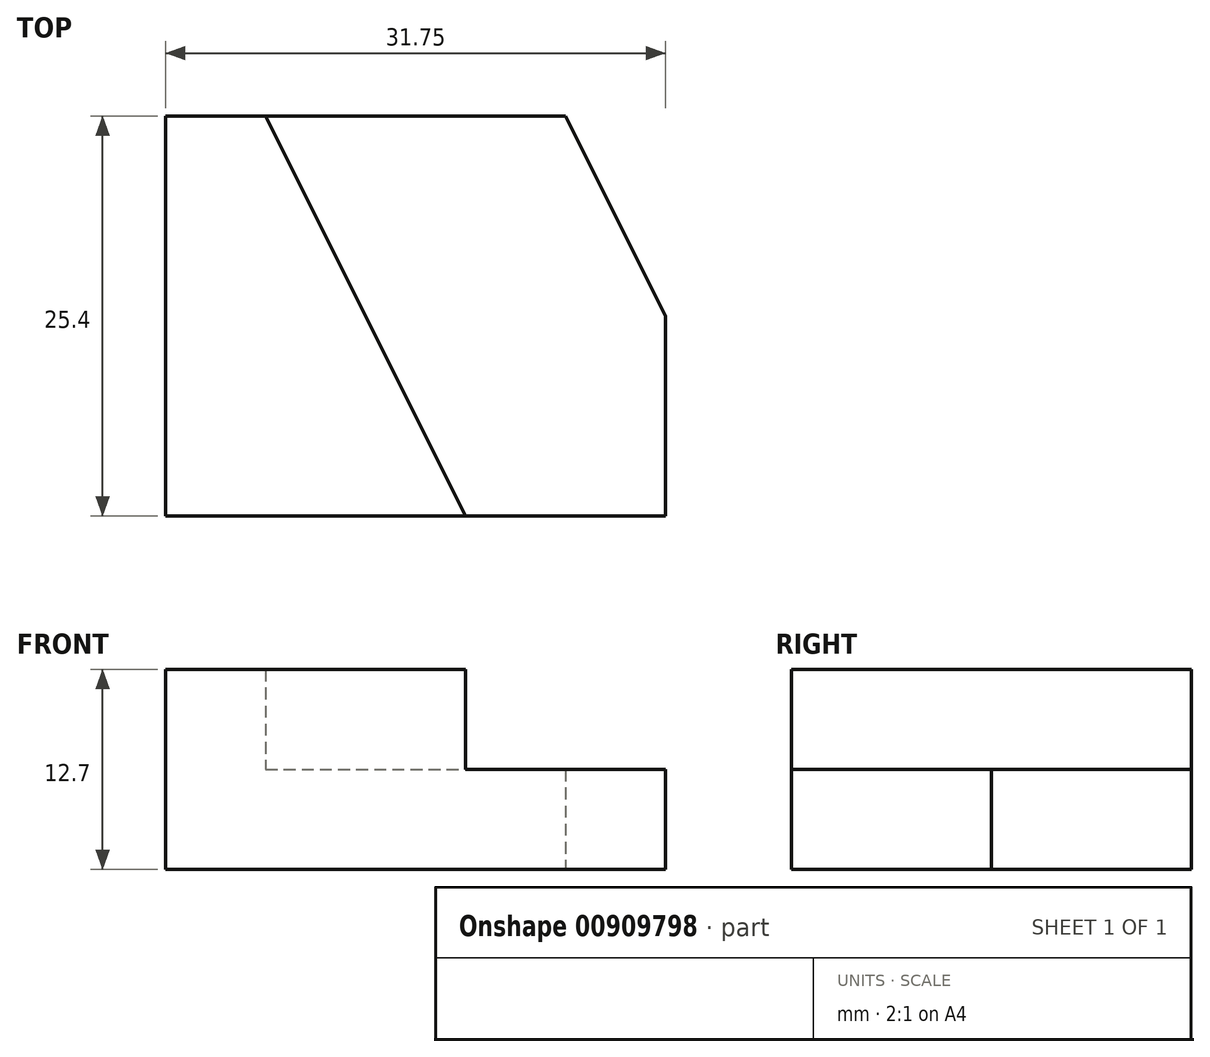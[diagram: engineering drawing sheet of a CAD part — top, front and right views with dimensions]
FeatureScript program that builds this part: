
annotation { "Feature Type Name" : "Feature", "Feature Type Description" : "" }
export const myFeature = defineFeature(function(context is Context, id is Id, definition is map)
    precondition{}
    {
        {
            var Q0;
            Q0=qCreatedBy(makeId("Top.planeOp"),FACE);
            var sketch = newSketch(context, id + "F0", { "sketchPlane" : qUnion([Q0])});
            skLineSegment(sketch, "E0", {"start": v(-58.15, 50.5) * mm, "end": v(-32.75, 50.5) * mm});
            skLineSegment(sketch, "E1", {"start": v(-58.15, 50.5) * mm, "end": v(-58.15, 25.1) * mm});
            skLineSegment(sketch, "E2", {"start": v(-58.15, 25.1) * mm, "end": v(-26.4, 25.1) * mm});
            skLineSegment(sketch, "E3", {"start": v(-26.4, 25.1) * mm, "end": v(-26.4, 37.8) * mm});
            skLineSegment(sketch, "E4", {"start": v(-32.75, 50.5) * mm, "end": v(-26.4, 37.8) * mm});
            skSolve(sketch);
        }
        {
            var Q0;
            Q0=makeQuery(id+"F0.imprint","IMPRINT",FACE,{"disambiguationData":[TD([[makeQuery(id+"F0.imprint","IMPRINT",EDGE,{"derivedFrom":sQuery(id+"F0.wireOp",EDGE,"E0")}),-1.0]])]});
            extrude(context, id + "F1", {"entities" : qUnion([Q0]), "depth" : 6.35 * mm, "offsetDistance" : 25.4 * mm});
        }
        {
            var Q0;
            Q0=makeQuery(id+"F1.opExtrude","CAP_FACE",FACE,{"disambiguationData":[OSD([sQuery(id+"F0.wireOp",EDGE,"E0"),sQuery(id+"F0.wireOp",EDGE,"E1"),sQuery(id+"F0.wireOp",EDGE,"E2"),sQuery(id+"F0.wireOp",EDGE,"E3"),sQuery(id+"F0.wireOp",EDGE,"E4")])],"isStart":false});
            var sketch = newSketch(context, id + "F2", { "sketchPlane" : qUnion([Q0])});
            skLineSegment(sketch, "E5", {"start": v(-58.15, 50.5) * mm, "end": v(-58.15, 25.1) * mm});
            skLineSegment(sketch, "E6", {"start": v(-58.15, 25.1) * mm, "end": v(-39.1, 25.1) * mm});
            skLineSegment(sketch, "E7", {"start": v(-58.15, 50.5) * mm, "end": v(-51.8, 50.5) * mm});
            skLineSegment(sketch, "E8", {"start": v(-51.8, 50.5) * mm, "end": v(-39.1, 25.1) * mm});
            skSolve(sketch);
        }
        {
            var Q0;
            Q0=makeQuery(id+"F2.imprint","IMPRINT",FACE,{"disambiguationData":[TD([[makeQuery(id+"F2.imprint","IMPRINT",EDGE,{"derivedFrom":sQuery(id+"F2.wireOp",EDGE,"E5")}),1.0]])]});
            extrude(context, id + "F3", {"entities" : qUnion([Q0]), "operationType" : NewBodyOperationType.ADD, "depth" : 6.35 * mm, "offsetDistance" : 25.4 * mm});
        }
    });
